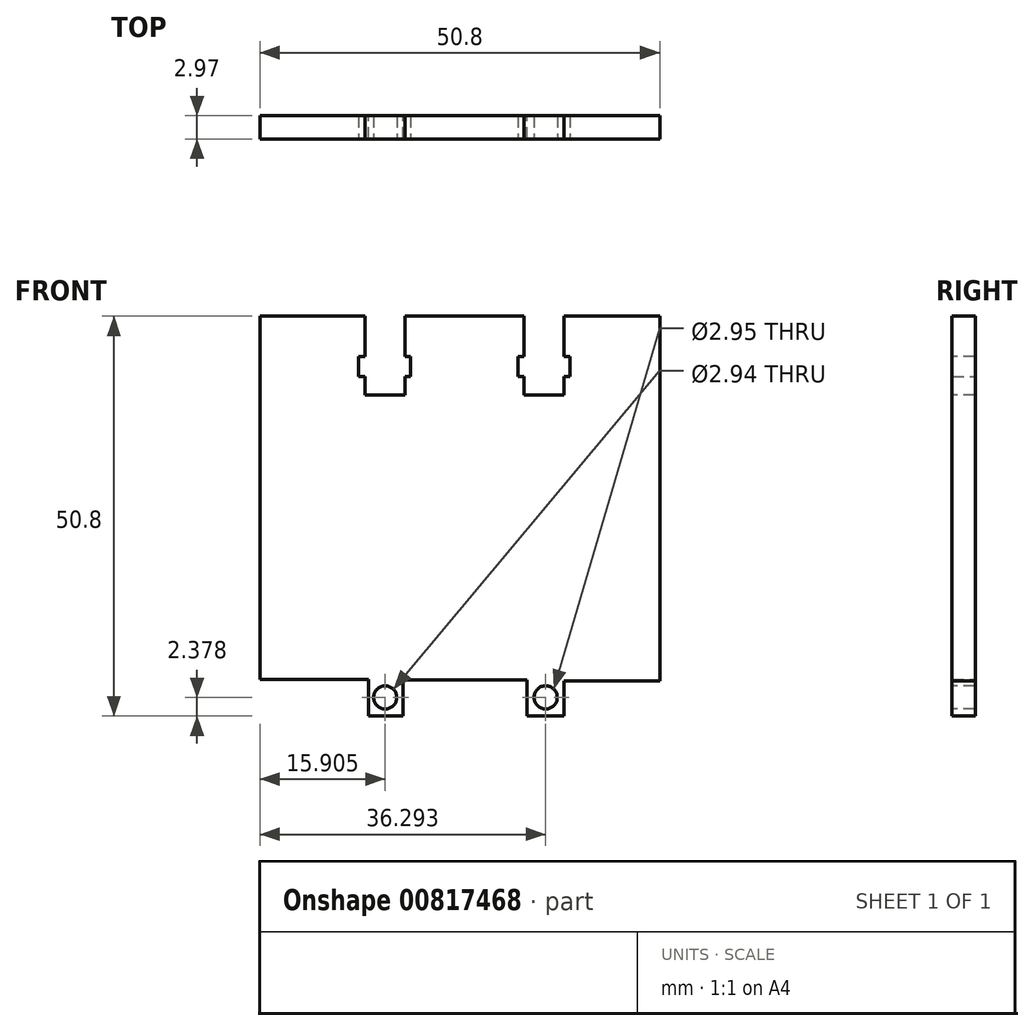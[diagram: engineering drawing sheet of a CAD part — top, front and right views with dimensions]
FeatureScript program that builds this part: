
annotation { "Feature Type Name" : "Feature", "Feature Type Description" : "" }
export const myFeature = defineFeature(function(context is Context, id is Id, definition is map)
    precondition{}
    {
        {
            var Q0;
            Q0=qCreatedBy(makeId("Front.planeOp"),FACE);
            var sketch = newSketch(context, id + "F0", { "sketchPlane" : qUnion([Q0])});
            skLineSegment(sketch, "E0.bottom", {"start": v(-25.98, 25.11) * mm, "end": v(24.82, 25.11) * mm});
            skLineSegment(sketch, "E0.top", {"start": v(-25.98, -25.69) * mm, "end": v(24.82, -25.69) * mm});
            skLineSegment(sketch, "E0.left", {"start": v(-25.98, 25.11) * mm, "end": v(-25.98, -25.69) * mm});
            skLineSegment(sketch, "E0.right", {"start": v(24.82, 25.11) * mm, "end": v(24.82, -25.69) * mm});
            skSolve(sketch);
        }
        {
            var Q0;
            Q0=makeQuery(id+"F0.imprint","IMPRINT",FACE,{"disambiguationData":[TD([[makeQuery(id+"F0.imprint","IMPRINT",EDGE,{"derivedFrom":sQuery(id+"F0.wireOp",EDGE,"E0.bottom")}),-1.0]])]});
            extrude(context, id + "F1", {"entities" : qUnion([Q0]), "depth" : 2.97 * mm, "offsetDistance" : 25.4 * mm});
        }
        {
            var Q0;
            Q0=makeQuery(id+"F1.opExtrude","CAP_FACE",FACE,{"disambiguationData":[OSD([sQuery(id+"F0.wireOp",EDGE,"E0.bottom"),sQuery(id+"F0.wireOp",EDGE,"E0.top"),sQuery(id+"F0.wireOp",EDGE,"E0.left"),sQuery(id+"F0.wireOp",EDGE,"E0.right")])],"isStart":false});
            var sketch = newSketch(context, id + "F2", { "sketchPlane" : qUnion([Q0])});
            skLineSegment(sketch, "E1.bottom", {"start": v(-12.66, 25.27) * mm, "end": v(-7.58, 25.27) * mm});
            skLineSegment(sketch, "E1.top", {"start": v(-12.66, 15.1) * mm, "end": v(-7.58, 15.1) * mm});
            skLineSegment(sketch, "E1.left", {"start": v(-12.66, 25.27) * mm, "end": v(-12.66, 15.1) * mm});
            skLineSegment(sketch, "E1.right", {"start": v(-7.58, 25.27) * mm, "end": v(-7.58, 15.1) * mm});
            skLineSegment(sketch, "E2.MirrorCS", {"start": v(9.6, 25.27) * mm, "end": v(9.6, 15.1) * mm});
            skLineSegment(sketch, "E3.MirrorCS", {"start": v(12.66, 25.27) * mm, "end": v(7.58, 25.27) * mm});
            skLineSegment(sketch, "E4.MirrorCS", {"start": v(12.66, 25.27) * mm, "end": v(12.66, 15.1) * mm});
            skLineSegment(sketch, "E5.MirrorCS", {"start": v(12.66, 15.1) * mm, "end": v(7.58, 15.1) * mm});
            skLineSegment(sketch, "E6.MirrorCS", {"start": v(26.8, 25.27) * mm, "end": v(26.8, 15.1) * mm});
            skLineSegment(sketch, "E7.MirrorCS", {"start": v(7.58, 25.27) * mm, "end": v(7.58, 15.1) * mm});
            skSolve(sketch);
        }
        {
            var Q0;
            Q0 = qSketchRegion(id + "F2", true);
            extrude(context, id + "F3", {"entities" : qUnion([Q0]), "operationType" : NewBodyOperationType.REMOVE, "oppositeDirection" : true, "depth" : 2.97 * mm, "offsetDistance" : 25.4 * mm});
        }
        {
            var Q0;
            Q0=makeQuery(id+"F1.opExtrude","CAP_FACE",FACE,{"disambiguationData":[OSD([sQuery(id+"F0.wireOp",EDGE,"E0.bottom"),sQuery(id+"F0.wireOp",EDGE,"E0.top"),sQuery(id+"F0.wireOp",EDGE,"E0.left"),sQuery(id+"F0.wireOp",EDGE,"E0.right")])],"isStart":false});
            var sketch = newSketch(context, id + "F4", { "sketchPlane" : qUnion([Q0])});
            skLineSegment(sketch, "E8.bottom", {"start": v(-6.84, 20) * mm, "end": v(-13.45, 20) * mm});
            skLineSegment(sketch, "E8.top", {"start": v(-6.84, 17.47) * mm, "end": v(-13.45, 17.47) * mm});
            skLineSegment(sketch, "E8.left", {"start": v(-6.84, 20) * mm, "end": v(-6.84, 17.47) * mm});
            skLineSegment(sketch, "E8.right", {"start": v(-13.45, 20) * mm, "end": v(-13.45, 17.47) * mm});
            skPoint(sketch, "E8.middle", {"position": v(-10.96, 20.1) * mm});
            skPoint(sketch, "E8.middle.positionSnap0", {"position": v(-12.66, 20.1) * mm});
            skPoint(sketch, "E8.centerSnap0", {"position": v(-12.66, 20.1) * mm});
            skLineSegment(sketch, "E9.MirrorCS", {"start": v(6.82, 17.47) * mm, "end": v(13.42, 17.47) * mm});
            skLineSegment(sketch, "E10.MirrorCS", {"start": v(6.82, 20) * mm, "end": v(6.82, 17.47) * mm});
            skLineSegment(sketch, "E11.MirrorCS", {"start": v(6.82, 20) * mm, "end": v(13.42, 20) * mm});
            skLineSegment(sketch, "E12.MirrorCS", {"start": v(13.42, 20) * mm, "end": v(13.42, 17.47) * mm});
            skSolve(sketch);
        }
        {
            var Q0;
            Q0 = qSketchRegion(id + "F4", true);
            extrude(context, id + "F5", {"entities" : qUnion([Q0]), "operationType" : NewBodyOperationType.REMOVE, "oppositeDirection" : true, "depth" : 2.97 * mm, "offsetDistance" : 25.4 * mm});
        }
        {
            var Q0;
            Q0=makeQuery(id+"F1.opExtrude","CAP_FACE",FACE,{"disambiguationData":[OSD([sQuery(id+"F0.wireOp",EDGE,"E0.bottom"),sQuery(id+"F0.wireOp",EDGE,"E0.top"),sQuery(id+"F0.wireOp",EDGE,"E0.left"),sQuery(id+"F0.wireOp",EDGE,"E0.right")])],"isStart":true});
            var sketch = newSketch(context, id + "F6", { "sketchPlane" : qUnion([Q0])});
            skLineSegment(sketch, "E13.bottom", {"start": v(-12.39, -21.22) * mm, "end": v(-24.82, -21.22) * mm});
            skLineSegment(sketch, "E13.top", {"start": v(-12.39, -25.69) * mm, "end": v(-24.82, -25.69) * mm});
            skLineSegment(sketch, "E13.left", {"start": v(-12.66, -21.22) * mm, "end": v(-12.66, -25.69) * mm});
            skLineSegment(sketch, "E13.right", {"start": v(-24.82, -21.22) * mm, "end": v(-24.82, -25.69) * mm});
            skSolve(sketch);
        }
        {
            var Q0;
            Q0=makeQuery(id+"F6.imprint","IMPRINT",FACE,{"disambiguationData":[TD([[makeQuery(id+"F6.imprint","IMPRINT",EDGE,{"derivedFrom":sQuery(id+"F6.wireOp",EDGE,"E13.bottom")}),1.0]])]});
            extrude(context, id + "F7", {"entities" : qUnion([Q0]), "operationType" : NewBodyOperationType.REMOVE, "oppositeDirection" : true, "depth" : 2.97 * mm, "offsetDistance" : 25.4 * mm});
        }
        {
            var Q0;
            Q0=makeQuery(id+"F1.opExtrude","CAP_FACE",FACE,{"disambiguationData":[OSD([sQuery(id+"F0.wireOp",EDGE,"E0.bottom"),sQuery(id+"F0.wireOp",EDGE,"E0.top"),sQuery(id+"F0.wireOp",EDGE,"E0.left"),sQuery(id+"F0.wireOp",EDGE,"E0.right")])],"isStart":true});
            var sketch = newSketch(context, id + "F8", { "sketchPlane" : qUnion([Q0])});
            skLineSegment(sketch, "E14.bottom", {"start": v(-10.22, -21.09) * mm, "end": v(10.16, -21.09) * mm});
            skLineSegment(sketch, "E14.top", {"start": v(-10.22, -25.69) * mm, "end": v(10.16, -25.69) * mm});
            skLineSegment(sketch, "E14.left", {"start": v(-7.93, -21.09) * mm, "end": v(-7.93, -25.69) * mm});
            skLineSegment(sketch, "E14.right", {"start": v(7.8, -21.09) * mm, "end": v(7.8, -25.69) * mm});
            skSolve(sketch);
        }
        {
            var Q0;
            Q0=makeQuery(id+"F8.imprint","IMPRINT",FACE,{"disambiguationData":[TD([[makeQuery(id+"F8.imprint","IMPRINT",EDGE,{"derivedFrom":sQuery(id+"F8.wireOp",EDGE,"E14.bottom")}),-1.0]])]});
            extrude(context, id + "F9", {"entities" : qUnion([Q0]), "operationType" : NewBodyOperationType.REMOVE, "oppositeDirection" : true, "depth" : 2.97 * mm, "offsetDistance" : 25.4 * mm});
        }
        {
            var Q0;
            Q0=makeQuery(id+"F1.opExtrude","CAP_FACE",FACE,{"disambiguationData":[OSD([sQuery(id+"F0.wireOp",EDGE,"E0.bottom"),sQuery(id+"F0.wireOp",EDGE,"E0.top"),sQuery(id+"F0.wireOp",EDGE,"E0.left"),sQuery(id+"F0.wireOp",EDGE,"E0.right")])],"isStart":true});
            var sketch = newSketch(context, id + "F10", { "sketchPlane" : qUnion([Q0])});
            skLineSegment(sketch, "E15.bottom", {"start": v(12.21, -21.04) * mm, "end": v(25.98, -21.04) * mm});
            skLineSegment(sketch, "E15.top", {"start": v(12.21, -25.69) * mm, "end": v(25.98, -25.69) * mm});
            skLineSegment(sketch, "E15.left", {"start": v(12.21, -21.04) * mm, "end": v(12.21, -25.69) * mm});
            skLineSegment(sketch, "E15.right", {"start": v(25.98, -21.62) * mm, "end": v(25.98, -25.69) * mm});
            skSolve(sketch);
        }
        {
            var Q0;
            {var subQ1=sQuery(id+"F10.wireOp",EDGE,"E15.bottom");Q0=makeQuery(id+"F10.imprint","IMPRINT",FACE,{"disambiguationData":[TD([[makeQuery(id+"F10.imprint","IMPRINT",EDGE,{"derivedFrom":subQ1}),-1.0]])]});}
            extrude(context, id + "F11", {"entities" : qUnion([Q0]), "operationType" : NewBodyOperationType.REMOVE, "oppositeDirection" : true, "depth" : 2.97 * mm, "offsetDistance" : 25.4 * mm});
        }
        {
            var Q0;
            Q0=makeQuery(id+"F1.opExtrude","CAP_FACE",FACE,{"disambiguationData":[OSD([sQuery(id+"F0.wireOp",EDGE,"E0.bottom"),sQuery(id+"F0.wireOp",EDGE,"E0.top"),sQuery(id+"F0.wireOp",EDGE,"E0.left"),sQuery(id+"F0.wireOp",EDGE,"E0.right")])],"isStart":false});
            var sketch = newSketch(context, id + "F12", { "sketchPlane" : qUnion([Q0])});
            skCircle(sketch, "E16", {"center": v(-10.08, -23.31) * mm, "radius": 1.47 * mm});
            skCircle(sketch, "E17", {"center": v(10.31, -23.31) * mm, "radius": 1.47 * mm});
            skSolve(sketch);
        }
        {
            var Q0;
            Q0 = qSketchRegion(id + "F12", true);
            extrude(context, id + "F13", {"entities" : qUnion([Q0]), "operationType" : NewBodyOperationType.REMOVE, "oppositeDirection" : true, "depth" : 2.97 * mm, "offsetDistance" : 25.4 * mm});
        }
    });
